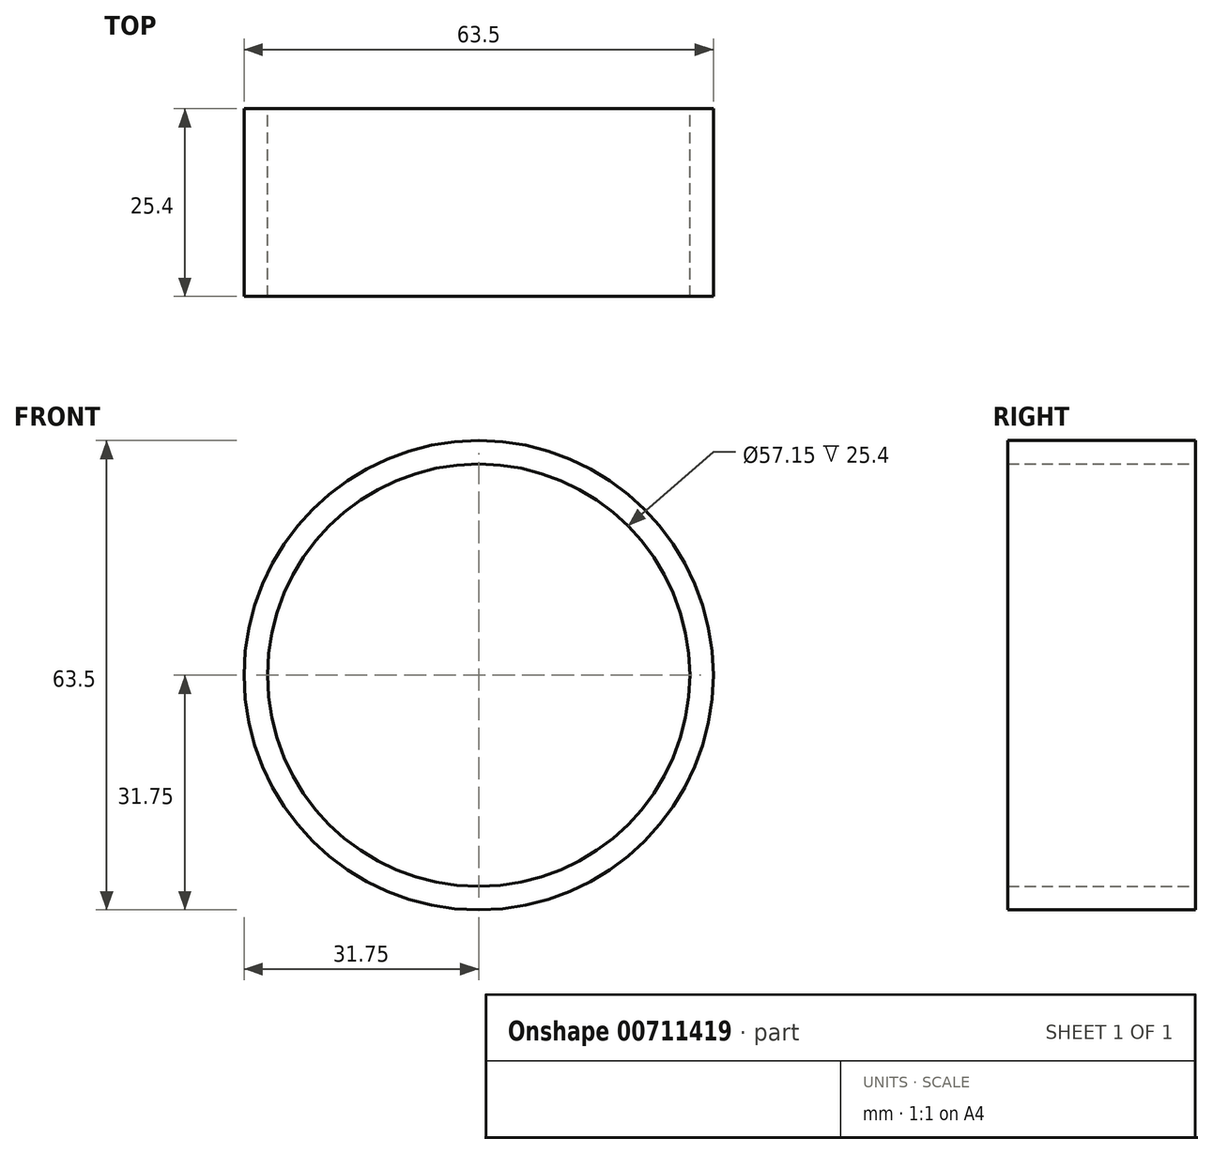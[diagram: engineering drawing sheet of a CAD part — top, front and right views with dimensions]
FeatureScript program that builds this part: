
annotation { "Feature Type Name" : "Feature", "Feature Type Description" : "" }
export const myFeature = defineFeature(function(context is Context, id is Id, definition is map)
    precondition{}
    {
        {
            var Q0;
            Q0=qCreatedBy(makeId("Front.planeOp"),FACE);
            var sketch = newSketch(context, id + "F0", { "sketchPlane" : qUnion([Q0])});
            skCircle(sketch, "E0", {"center": v(0, 0) * mm, "radius": 31.75 * mm});
            skCircle(sketch, "E1", {"center": v(0, 0) * mm, "radius": 28.58 * mm});
            skSolve(sketch);
        }
        {
            var Q0;
            Q0 = qSketchRegion(id + "F0", true);
            extrude(context, id + "F1", {"entities" : qUnion([Q0]), "depth" : 25.4 * mm, "offsetDistance" : 25.4 * mm});
        }
    });
